# Revit family: NLRS_33_RB_DO_BILCO_dakluik_ESW-50REM
name_source: partatom
category: Doors
revit_build: Autodesk Revit 2015 (Build: 20140223_1515(x64)
units: mm (PartAtom-declared; Revit-internal decimal feet)

## types (1)
- SmokeVentESW-50REM
    Description = rookluik ESW-50-REM
    Height = 375 mm  [stored 1.23031 ft]
    IfcExportAs = IfcDoor
    IfcExportType = NOTDEFINED
    Length = 1488 mm  [stored 4.88189 ft]
    Manufacturer = Bilco
    Model = ESW50REM
    RWA = Yes
    Rough Height = 0 mm  [stored 0 ft]
    Rough Width = 0 mm  [stored 0 ft]
    Thickness = 0 mm  [stored 0 ft]
    Width = 1488 mm  [stored 4.88189 ft]
    aansluiting BMC = Yes
    bediening = elektrisch
    brandwerend 60 min = No
    breedte = 1488 mm  [stored 4.88189 ft]
    breedte paneel = 1364 mm  [stored 4.47507 ft]
    breuklast kN = 0
    code productgroep = LUI
    conservering = brut
    dagmaatbreedte = 1260 mm  [stored 4.13386 ft]
    dagmaatlengte = 1260 mm  [stored 4.13386 ft]
    gewicht = 0
    hoogte = 375 mm  [stored 1.23031 ft]
    hoogte opstand = 305 mm  [stored 1.00066 ft]
    isolatiewaarde = 2.13
    lengte = 1488 mm  [stored 4.88189 ft]
    lengte paneel = 1364 mm  [stored 4.47507 ft]
    materiaal = bcb_aluminium
    materiaal_paneel = bcb_aluminium
    materiaal_rand = bcb_aluminium
    normering = EN12101-2
    omranding = Yes
    omranding hoekprofiel = No
    omranding waterafvoerend = No
    omschrijving = rookluik ESW-50-REM
    openingshoek = 140.00°
    openstand vergrendeling = No
    productgroep = Dakluiken
    scharnierend = Yes
    sluiting_inbus = 0
    thermische onderbreking = No
    waterdicht = Yes
    windweerstand = WL 1500

note: [stored X ft] marks values corroborated as IEEE doubles in the binary element streams (Revit-internal decimal feet)

## geometry (parser evidence)
native form markers: Blend x4, Sweep x7
no freeform markers — native parametric forms only
